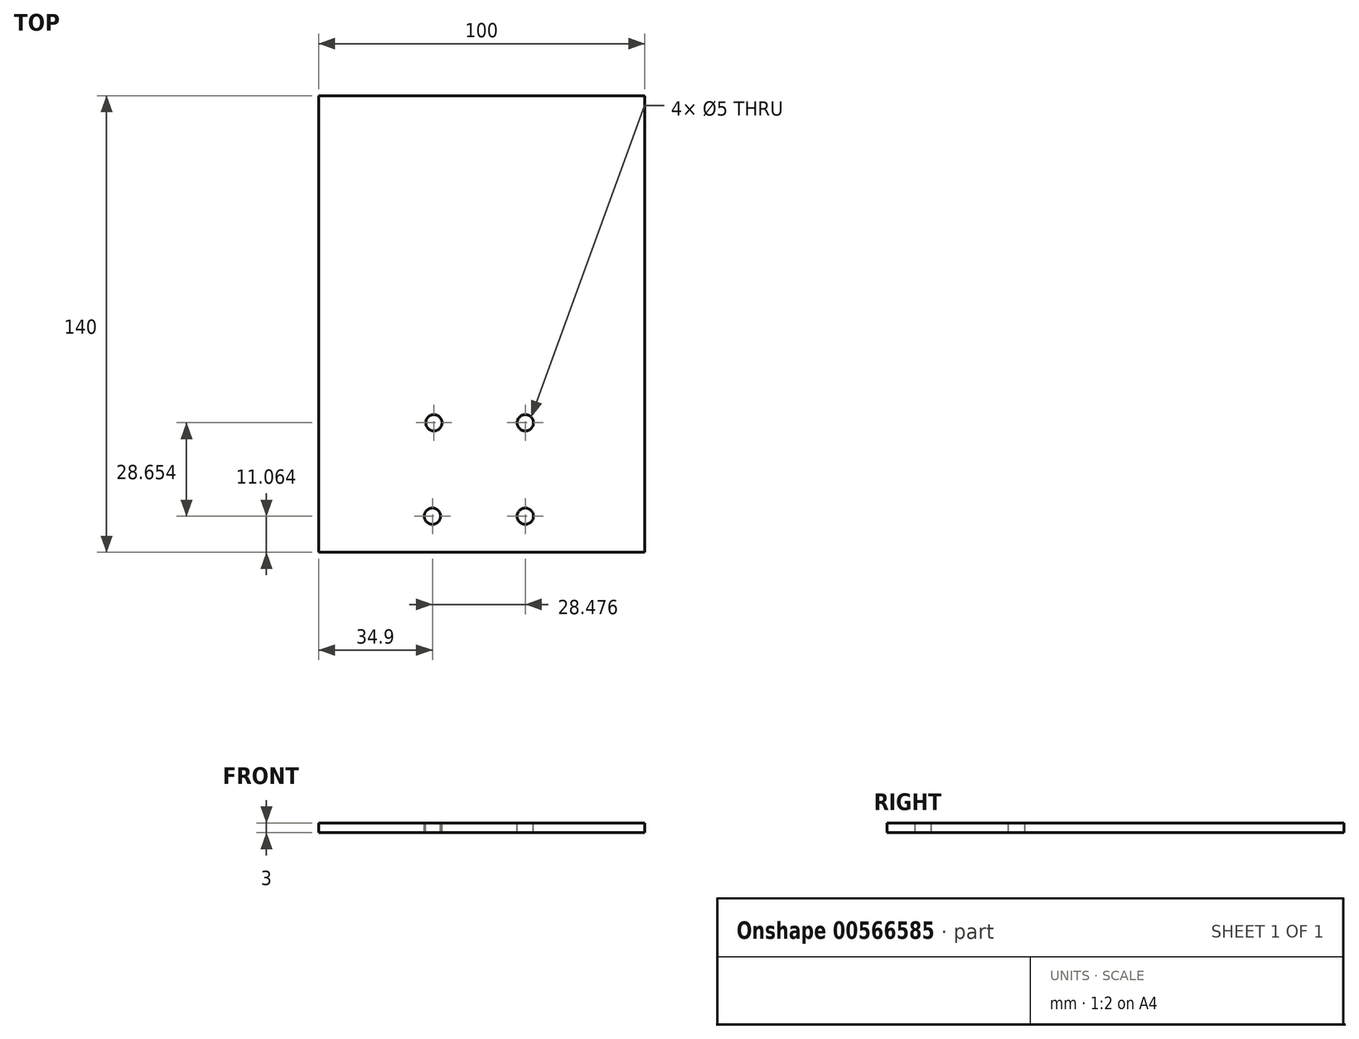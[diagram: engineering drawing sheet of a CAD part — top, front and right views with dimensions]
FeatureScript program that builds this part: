
annotation { "Feature Type Name" : "Feature", "Feature Type Description" : "" }
export const myFeature = defineFeature(function(context is Context, id is Id, definition is map)
    precondition{}
    {
        {
            var Q0;
            Q0=qCreatedBy(makeId("Top.planeOp"),FACE);
            var sketch = newSketch(context, id + "F0", { "sketchPlane" : qUnion([Q0])});
            skLineSegment(sketch, "E0.bottom", {"start": v(0, -99.34) * mm, "end": v(100, -99.34) * mm});
            skLineSegment(sketch, "E0.top", {"start": v(0, 40.66) * mm, "end": v(100, 40.66) * mm});
            skLineSegment(sketch, "E0.left", {"start": v(0, -99.34) * mm, "end": v(0, 40.66) * mm});
            skLineSegment(sketch, "E0.right", {"start": v(100, -99.34) * mm, "end": v(100, 40.66) * mm});
            skSolve(sketch);
        }
        {
            var Q0;
            Q0 = qSketchRegion(id + "F0", true);
            var sketch = newSketch(context, id + "F1", { "sketchPlane" : qUnion([Q0])});
            skSolve(sketch);
        }
        {
            var Q0;
            Q0=makeQuery(id+"F1.imprint","IMPRINT",FACE,{"disambiguationData":[TD([[makeQuery(id+"F1.imprint","IMPRINT",EDGE,{"derivedFrom":makeQuery(id+"F0.imprint","IMPRINT",EDGE,{"derivedFrom":sQuery(id+"F0.wireOp",EDGE,"E0.bottom")})}),1.0]])]});
            extrude(context, id + "F2", {"entities" : qUnion([Q0]), "depth" : 3 * mm, "offsetDistance" : 25.4 * mm});
        }
        {
            var Q0;
            Q0=makeQuery(id+"F2.opExtrude","CAP_FACE",FACE,{"disambiguationData":[OSD([sQuery(id+"F0.wireOp",EDGE,"E0.bottom"),sQuery(id+"F0.wireOp",EDGE,"E0.top"),sQuery(id+"F0.wireOp",EDGE,"E0.left"),sQuery(id+"F0.wireOp",EDGE,"E0.right")])],"isStart":false});
            var sketch = newSketch(context, id + "F3", { "sketchPlane" : qUnion([Q0])});
            skLineSegment(sketch, "E1.bottom", {"start": v(0, 0) * mm, "end": v(11.58, 0) * mm});
            skLineSegment(sketch, "E1.top", {"start": v(0, -41.76) * mm, "end": v(11.58, -41.76) * mm});
            skLineSegment(sketch, "E1.left", {"start": v(0, 0) * mm, "end": v(0, -41.76) * mm});
            skLineSegment(sketch, "E1.right", {"start": v(11.58, 0) * mm, "end": v(11.58, -41.76) * mm});
            skLineSegment(sketch, "E2.bottom", {"start": v(100, 0) * mm, "end": v(89.2, 0) * mm});
            skLineSegment(sketch, "E2.top", {"start": v(100, -41.56) * mm, "end": v(89.2, -41.56) * mm});
            skLineSegment(sketch, "E2.left", {"start": v(100, 0) * mm, "end": v(100, -41.56) * mm});
            skLineSegment(sketch, "E2.right", {"start": v(89.2, 0) * mm, "end": v(89.2, -41.56) * mm});
            skSolve(sketch);
        }
        {
            var Q0;
            Q0 = qSketchRegion(id + "F3", true);
            var sketch = newSketch(context, id + "F4", { "sketchPlane" : qUnion([Q0])});
            skLineSegment(sketch, "E3", {"start": v(98.31, -41.16) * mm, "end": v(98.31, 0) * mm});
            skSolve(sketch);
        }
        {
            var Q0;
            Q0=sQuery(id+"F4.wireOp",EDGE,"E3");
            var Q1;
            Q1=sQuery(id+"F3.wireOp",EDGE,"E1.left");
            extrude(context, id + "F5", {"bodyType" : ToolBodyType.SURFACE, "surfaceEntities" : qUnion([Q0, Q1]), "depth" : 10 * mm, "offsetDistance" : 25.4 * mm});
        }
        {
            var Q0;
            Q0=makeQuery(id+"F2.opExtrude","CAP_FACE",FACE,{"disambiguationData":[OSD([sQuery(id+"F0.wireOp",EDGE,"E0.bottom"),sQuery(id+"F0.wireOp",EDGE,"E0.top"),sQuery(id+"F0.wireOp",EDGE,"E0.left"),sQuery(id+"F0.wireOp",EDGE,"E0.right")])],"isStart":false});
            var sketch = newSketch(context, id + "F6", { "sketchPlane" : qUnion([Q0])});
            skLineSegment(sketch, "E4", {"start": v(34.9, -88.28) * mm, "end": v(63.38, -88.28) * mm});
            skLineSegment(sketch, "E5", {"start": v(63.38, -88.28) * mm, "end": v(63.38, -59.62) * mm});
            skLineSegment(sketch, "E6", {"start": v(63.38, -59.62) * mm, "end": v(35.35, -59.62) * mm});
            skLineSegment(sketch, "E7", {"start": v(35.35, -59.62) * mm, "end": v(34.9, -88.28) * mm});
            skSolve(sketch);
        }
        {
            var Q0;
            Q0=sQuery(id+"F6.wireOp",VERTEX,"E7.start");
            var Q1;
            Q1=sQuery(id+"F6.wireOp",VERTEX,"E7.end");
            var Q2;
            Q2=sQuery(id+"F6.wireOp",VERTEX,"E6.start");
            var Q3;
            Q3=sQuery(id+"F6.wireOp",VERTEX,"E5.start");
            var Q4;
            Q4=makeQuery(id+"F2.opExtrude","SWEPT_BODY",BODY,{"disambiguationData":[OSD([sQuery(id+"F0.wireOp",EDGE,"E0.bottom"),sQuery(id+"F0.wireOp",EDGE,"E0.top"),sQuery(id+"F0.wireOp",EDGE,"E0.left"),sQuery(id+"F0.wireOp",EDGE,"E0.right")])]});
            hole(context, id + "F7", {"style" : HoleStyle.SIMPLE, "endStyle" : HoleEndStyle.THROUGH, "holeDiameter" : 5 * mm, "isTappedThrough" : true, "tappedDepth" : 12.7 * mm, "tapClearance" : 3, "locations" : qUnion([Q0, Q1, Q2, Q3]), "scope" : qUnion([Q4])});
        }
    });
